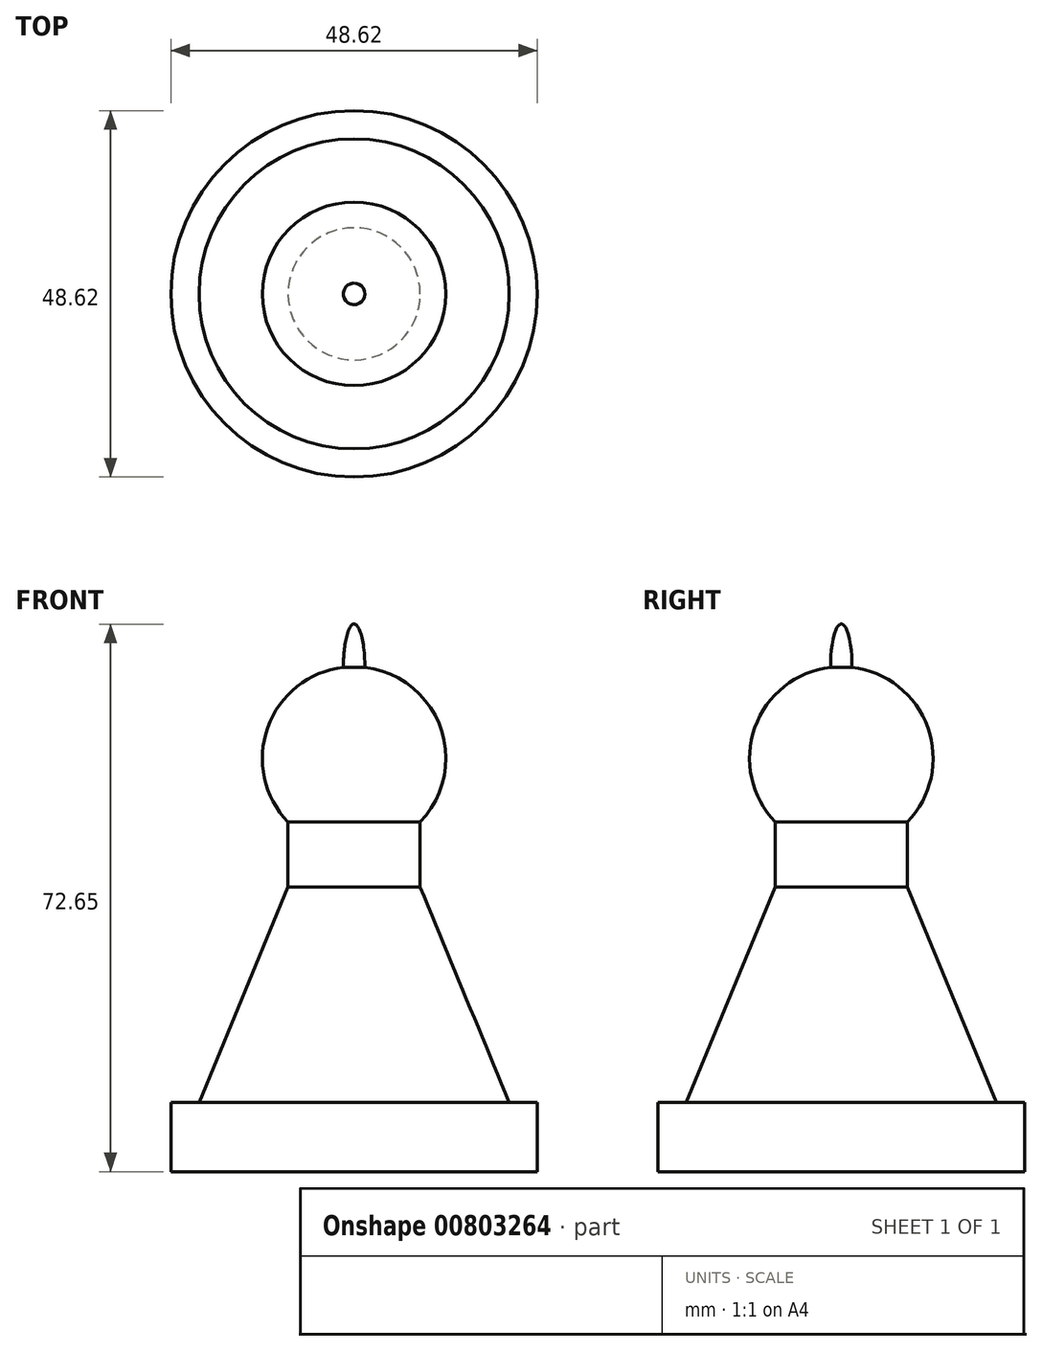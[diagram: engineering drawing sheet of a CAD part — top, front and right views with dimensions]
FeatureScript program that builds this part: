
annotation { "Feature Type Name" : "Feature", "Feature Type Description" : "" }
export const myFeature = defineFeature(function(context is Context, id is Id, definition is map)
    precondition{}
    {
        {
            var Q0;
            Q0=qCreatedBy(makeId("Front.planeOp"),FACE);
            var sketch = newSketch(context, id + "F0", { "sketchPlane" : qUnion([Q0])});
            skLineSegment(sketch, "E0", {"start": v(0, 77.9) * mm, "end": v(0, -77.15) * mm, "construction": true});
            skLineSegment(sketch, "E1.bottom", {"start": v(0, -54.82) * mm, "end": v(24.31, -54.82) * mm});
            skLineSegment(sketch, "E1.top", {"start": v(20.56, -45.62) * mm, "end": v(24.31, -45.62) * mm});
            skLineSegment(sketch, "E1.right", {"start": v(24.31, -54.82) * mm, "end": v(24.31, -45.62) * mm});
            skLineSegment(sketch, "E2", {"start": v(8.77, -17.09) * mm, "end": v(8.77, -8.06) * mm});
            skLineSegment(sketch, "E3", {"start": v(8.77, -17.09) * mm, "end": v(20.56, -45.62) * mm});
            skArc(sketch, "E4", {"start": v(8.77, -8.45) * mm, "mid": v(11.46, 4.1) * mm, "end": v(1.42, 12.1) * mm});
            skEllipticalArc(sketch, "E5", {});
            skLineSegment(sketch, "E6", {"start": v(0, 17.83) * mm, "end": v(0, -54.82) * mm});
            const initialGuessF0  = {"E5": [0, 0.012174921213205672, 0, 1, 0.005658810855332994, 0.001421423812953089, 4.697678232945746, 0]};
            skSetInitialGuess(sketch, initialGuessF0);
            skSolve(sketch);
        }
        {
            var Q0;
            Q0=makeQuery(id+"F0.imprint","IMPRINT",FACE,{"disambiguationData":[TD([[makeQuery(id+"F0.imprint","IMPRINT",EDGE,{"derivedFrom":sQuery(id+"F0.wireOp",EDGE,"E1.bottom")}),1.0]])]});
            var Q1;
            Q1=sQuery(id+"F0.wireOp",EDGE,"E0");
            revolve(context, id + "F1", {"surfaceOperationType" : NewSurfaceOperationType.NEW, "entities" : qUnion([Q0]), "axis" : qUnion([Q1]), "revolveType" : RevolveType.FULL});
        }
    });
